# Revit family: Alsanit - Kabiny sanitarne LIFT - HPL
name_source: partatom
category: Doors
units: mm (PartAtom-declared; Revit-internal decimal feet)

## family parameters
Always vertical = Yes
Cut with Voids When Loaded = No
Room Calculation Point = No
Shared = No
Work Plane-Based = No

## types (2) — shared parameters
Analytic Construction = <None>
Autor = www.archispace.pl
Construction Type = Kabiny sanitarne
Define Thermal Properties by = Schematic Type
Description = Kabiny sanitarne SOLARI to idealna kombinacja trwałości i estetyki w najnowszej cenie. Ze względu na estetyczność zastosowań jest najchętniej kupowanym systemem kabin sanitarnych w Polsce.
Film Instruktażowy = https://youtu.be
Function = Interior
Krótki opis = Kabiny sanitarne ALSANIT posiadające oznaczenie CE zgodnie z parametrami systemu
Lewa strona połączona typ = Rodzaj połączenia : Połączona
Lewa strona przy ścianie typ = Rodzaj połączenia : Przy ścianie
Lewa strona zamknięta typ = Rodzaj połączenia : Zamknięta
Manufacturer = Alsanit
Materiał belek = Alsanit - Aluminium
Materiał okuć = Alsanit - Aluminium
Materiał płyt = Alsanit - HPL - Biały 9016
Materiał wsporników = Alsanit - Aluminium
Model = SOLARI
Prawa strona połączona typ = Rodzaj połączenia : Połączona
Prawa strona przy ścianie typ = Rodzaj połączenia : Przy ścianie
Prawa strona zamknięta typ = Rodzaj połączenia : Zamknięta
Rodzaj płyt = HPL - Wysokociśnieniowy laminat kompaktowy
Stopka nóżki = 50 mm  [stored 0.164042 ft]
Type Comments = Kabiny sanitarne (ścianki giszetowe do WC)
URL = https://www.alsanit.pl
Średnica podpory górnej = 57 mm  [stored 0.187008 ft]
zero-valued in all types: Default Elevation, Height, Rough Height, Rough Width, Width

## per-type parameters (varying)
| type | Grubość ścianki | Thickness |
| 10 mm | 10 mm  [stored 0.0328084 ft] | 10 mm  [stored 0.0328084 ft] |
| 12 mm | 12 mm  [stored 0.0393701 ft] | 12 mm  [stored 0.0393701 ft] |

note: [stored X ft] marks values corroborated as IEEE doubles in the binary element streams (Revit-internal decimal feet)

## geometry (parser evidence)
native form markers: Sweep x9
no freeform markers — native parametric forms only
